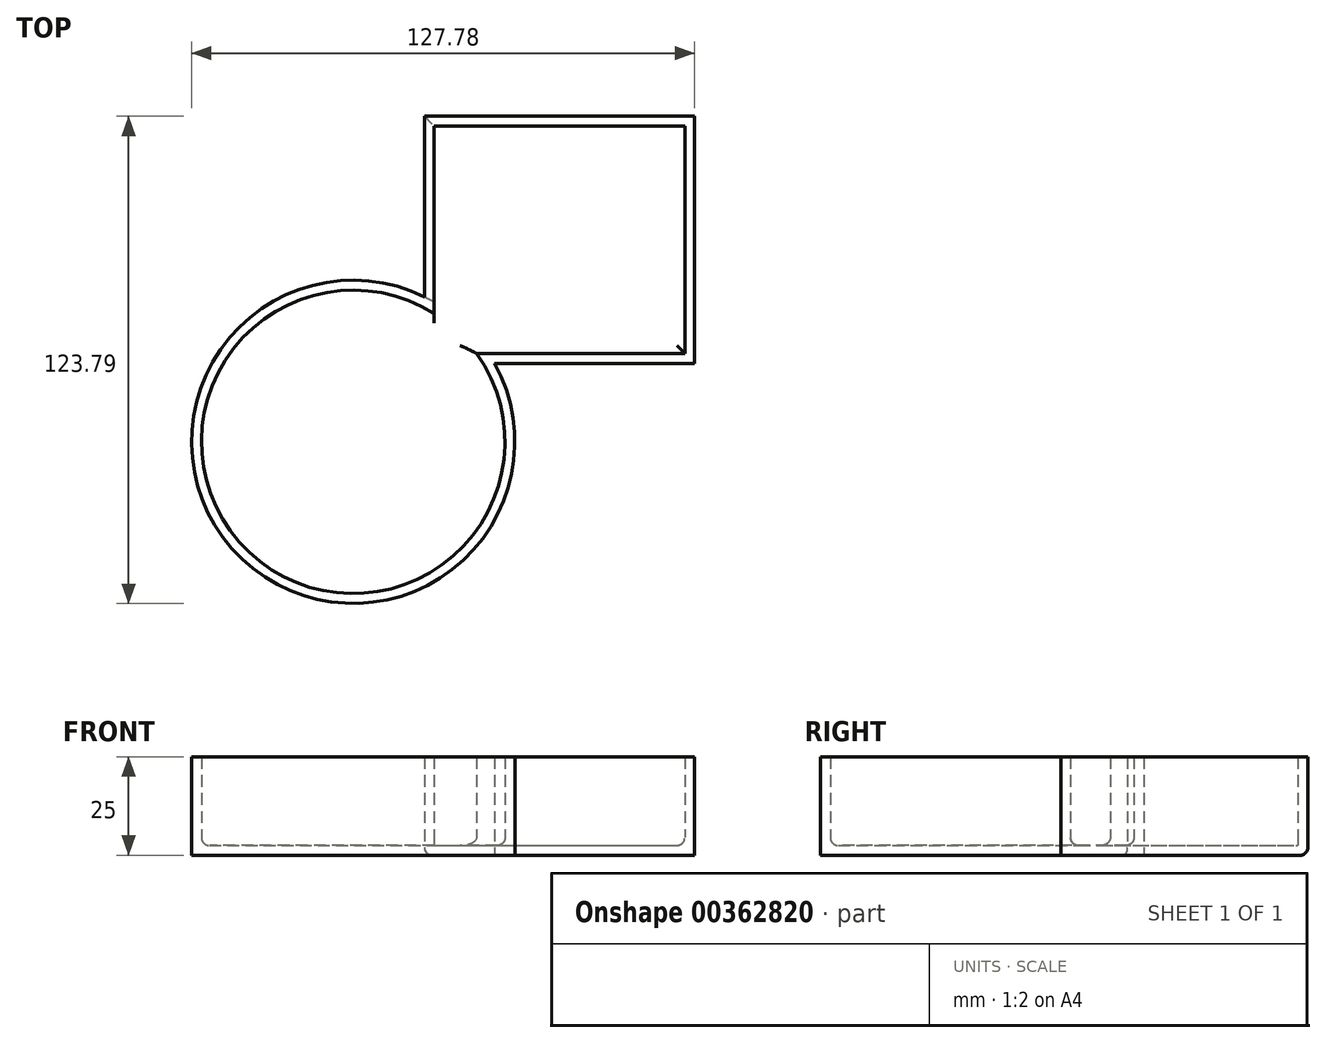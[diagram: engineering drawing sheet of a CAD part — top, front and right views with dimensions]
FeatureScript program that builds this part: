
annotation { "Feature Type Name" : "Feature", "Feature Type Description" : "" }
export const myFeature = defineFeature(function(context is Context, id is Id, definition is map)
    precondition{}
    {
        {
            var Q0;
            Q0=qCreatedBy(makeId("Top.planeOp"),FACE);
            var sketch = newSketch(context, id + "F0", { "sketchPlane" : qUnion([Q0])});
            skLineSegment(sketch, "E0.bottom", {"start": v(-19.8, -29.27) * mm, "end": v(31.05, -29.27) * mm});
            skLineSegment(sketch, "E0.top", {"start": v(-37.59, 33.52) * mm, "end": v(31.05, 33.52) * mm});
            skLineSegment(sketch, "E0.left", {"start": v(-37.59, -12.37) * mm, "end": v(-37.59, 33.52) * mm});
            skLineSegment(sketch, "E0.right", {"start": v(31.05, -29.27) * mm, "end": v(31.05, 33.52) * mm});
            skArc(sketch, "E1", {"start": v(-37.59, -12.37) * mm, "mid": v(-83.95, -78.98) * mm, "end": v(-19.8, -29.27) * mm});
            skLineSegment(sketch, "E2.0", {"start": v(2.3, -46.27) * mm, "end": v(48.05, -46.27) * mm});
            skArc(sketch, "E2.1", {"start": v(-54.59, 8.82) * mm, "mid": v(-96.06, -90.92) * mm, "end": v(2.3, -46.27) * mm});
            skLineSegment(sketch, "E2.2", {"start": v(48.05, -46.27) * mm, "end": v(48.05, 50.52) * mm});
            skLineSegment(sketch, "E2.3", {"start": v(-54.59, 50.52) * mm, "end": v(48.05, 50.52) * mm});
            skLineSegment(sketch, "E2.4", {"start": v(-54.59, 8.82) * mm, "end": v(-54.59, 50.52) * mm});
            skSolve(sketch);
        }
        {
            var Q0;
            Q0=makeQuery(id+"F0.imprint","IMPRINT",FACE,{"disambiguationData":[TD([[makeQuery(id+"F0.imprint","IMPRINT",EDGE,{"derivedFrom":sQuery(id+"F0.wireOp",EDGE,"E0.bottom")}),1.0]])]});
            extrude(context, id + "F1", {"entities" : qUnion([Q0]), "depth" : 25 * mm});
        }
        {
            var Q0;
            Q0=makeQuery(id+"F1.opExtrude","CAP_FACE",FACE,{"disambiguationData":[OSD([sQuery(id+"F0.wireOp",EDGE,"E0.bottom"),sQuery(id+"F0.wireOp",EDGE,"E0.top"),sQuery(id+"F0.wireOp",EDGE,"E0.left"),sQuery(id+"F0.wireOp",EDGE,"E0.right"),sQuery(id+"F0.wireOp",EDGE,"E1")])],"isStart":false});
            shell(context, id + "F2", {"entities" : qUnion([Q0]), "thickness" : 2.5 * mm});
        }
        {
            var Q0;
            {var subQ0=sQuery(id+"F0.wireOp",EDGE,"E1");Q0=makeQuery(id+"F2.opShell","OFFSET_EDGE",EDGE,{"disambiguationData":[OSD([subQ0]),TDD([makeQuery(id+"F1.opExtrude","CAP_EDGE",EDGE,{"disambiguationData":[OSD([subQ0])],"isStart":true})])]});}
            var Q1;
            Q1=makeQuery(id+"F1.opExtrude","CAP_EDGE",EDGE,{"disambiguationData":[OSD([sQuery(id+"F0.wireOp",EDGE,"E0.left")])],"isStart":true});
            var Q2;
            Q2=makeQuery(id+"F1.opExtrude","CAP_EDGE",EDGE,{"disambiguationData":[OSD([sQuery(id+"F0.wireOp",EDGE,"E0.top")])],"isStart":true});
            var Q3;
            {var subQ0=sQuery(id+"F0.wireOp",EDGE,"E0.right");Q3=makeQuery(id+"F2.opShell","OFFSET_EDGE",EDGE,{"disambiguationData":[OSD([subQ0]),TDD([makeQuery(id+"F1.opExtrude","CAP_EDGE",EDGE,{"disambiguationData":[OSD([subQ0])],"isStart":true})])]});}
            var Q4;
            {var subQ0=sQuery(id+"F0.wireOp",EDGE,"E0.bottom");Q4=makeQuery(id+"F2.opShell","OFFSET_EDGE",EDGE,{"disambiguationData":[OSD([subQ0]),TDD([makeQuery(id+"F1.opExtrude","CAP_EDGE",EDGE,{"disambiguationData":[OSD([subQ0])],"isStart":true})])]});}
            fillet(context, id + "F3", {"entities" : qUnion([Q0, Q1, Q2, Q3, Q4]), "radius" : 2 * mm, "tangentPropagation" : true, "allowEdgeOverflow" : false});
        }
    });
